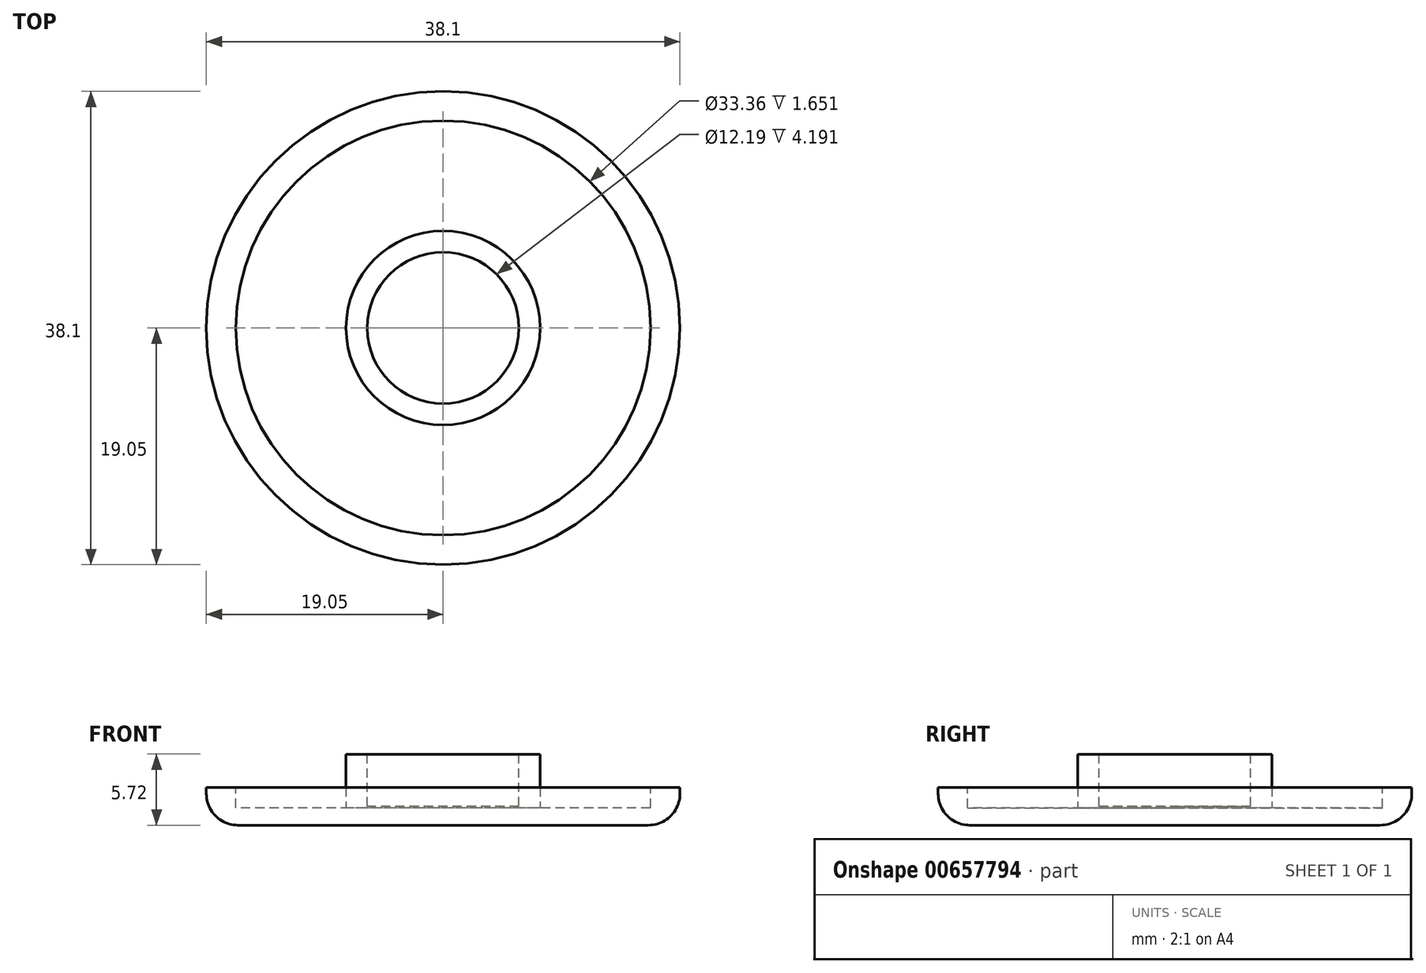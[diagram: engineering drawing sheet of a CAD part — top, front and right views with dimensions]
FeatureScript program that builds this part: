
annotation { "Feature Type Name" : "Feature", "Feature Type Description" : "" }
export const myFeature = defineFeature(function(context is Context, id is Id, definition is map)
    precondition{}
    {
        {
            var Q0;
            Q0=qCreatedBy(makeId("Top.planeOp"),FACE);
            var sketch = newSketch(context, id + "F0", { "sketchPlane" : qUnion([Q0])});
            skCircle(sketch, "E0", {"center": v(0, 0) * mm, "radius": 19.05 * mm});
            skSolve(sketch);
        }
        {
            var Q0;
            Q0=makeQuery(id+"F0.imprint","IMPRINT",FACE,{"disambiguationData":[TD([[makeQuery(id+"F0.imprint","IMPRINT",EDGE,{"derivedFrom":sQuery(id+"F0.wireOp",EDGE,"E0")}),1.0]])]});
            extrude(context, id + "F1", {"entities" : qUnion([Q0]), "depth" : 3.05 * mm, "offsetDistance" : 25.4 * mm});
        }
        {
            var Q0;
            Q0=makeQuery(id+"F1.opExtrude","CAP_EDGE",EDGE,{"disambiguationData":[OSD([sQuery(id+"F0.wireOp",EDGE,"E0")])],"isStart":true});
            fillet(context, id + "F2", {"entities" : qUnion([Q0]), "radius" : 2.54 * mm, "tangentPropagation" : true, "allowEdgeOverflow" : false});
        }
        {
            var Q0;
            Q0=makeQuery(id+"F1.opExtrude","CAP_FACE",FACE,{"disambiguationData":[OSD([sQuery(id+"F0.wireOp",EDGE,"E0")])],"isStart":false});
            var sketch = newSketch(context, id + "F3", { "sketchPlane" : qUnion([Q0])});
            skCircle(sketch, "E1", {"center": v(0, 0) * mm, "radius": 16.68 * mm});
            skSolve(sketch);
        }
        {
            var Q0;
            Q0 = qSketchRegion(id + "F3", true);
            extrude(context, id + "F4", {"entities" : qUnion([Q0]), "operationType" : NewBodyOperationType.REMOVE, "oppositeDirection" : true, "depth" : 1.65 * mm, "offsetDistance" : 25.4 * mm});
        }
        {
            var Q0;
            Q0=makeQuery(id+"F4.boolean.opBoolean","COPY",FACE,{"derivedFrom":makeQuery(id+"F4.opExtrude","CAP_FACE",FACE,{"disambiguationData":[OSD([sQuery(id+"F3.wireOp",EDGE,"E1")])],"isStart":false})});
            var sketch = newSketch(context, id + "F5", { "sketchPlane" : qUnion([Q0])});
            skCircle(sketch, "E2", {"center": v(0, 0) * mm, "radius": 7.81 * mm});
            skSolve(sketch);
        }
        {
            var Q0;
            Q0 = qSketchRegion(id + "F5", true);
            extrude(context, id + "F6", {"entities" : qUnion([Q0]), "operationType" : NewBodyOperationType.ADD, "depth" : 4.32 * mm, "offsetDistance" : 25.4 * mm});
        }
        {
            var Q0;
            Q0=makeQuery(id+"F6.opExtrude","CAP_FACE",FACE,{"disambiguationData":[OSD([sQuery(id+"F5.wireOp",EDGE,"E2")])],"isStart":false});
            var sketch = newSketch(context, id + "F7", { "sketchPlane" : qUnion([Q0])});
            skCircle(sketch, "E3", {"center": v(0, 0) * mm, "radius": 6.1 * mm});
            skSolve(sketch);
        }
        {
            var Q0;
            Q0 = qSketchRegion(id + "F7", true);
            extrude(context, id + "F8", {"entities" : qUnion([Q0]), "operationType" : NewBodyOperationType.REMOVE, "oppositeDirection" : true, "depth" : 4.2 * mm, "offsetDistance" : 25.4 * mm});
        }
    });
